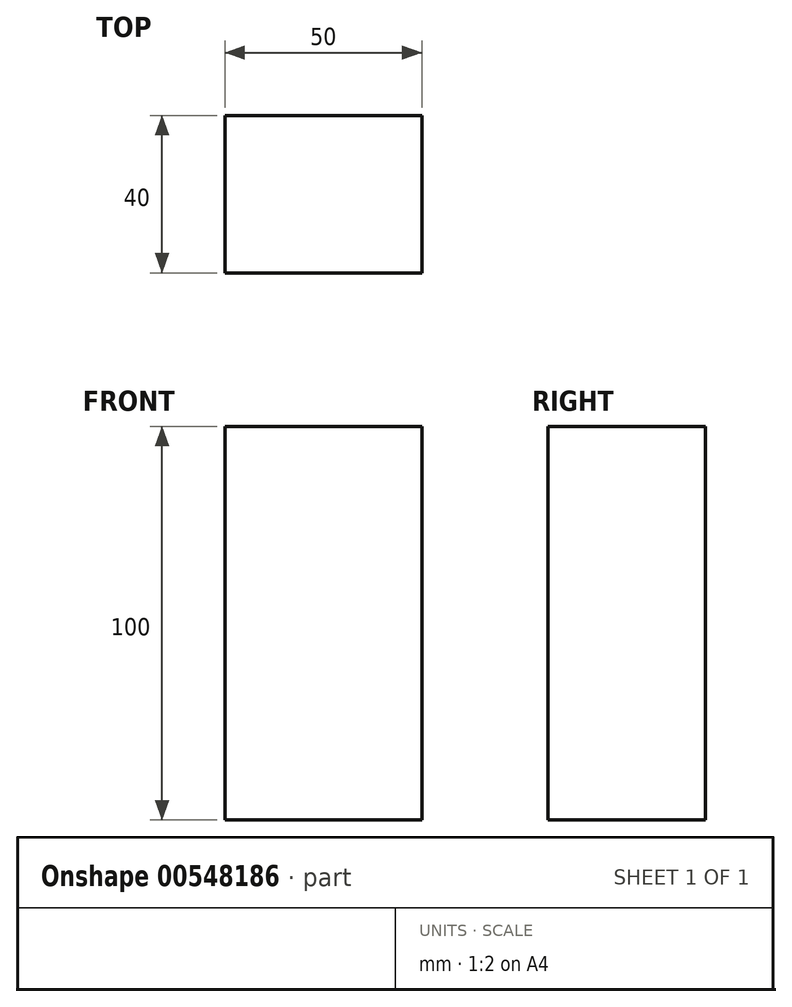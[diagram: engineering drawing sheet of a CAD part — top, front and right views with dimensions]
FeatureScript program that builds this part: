
annotation { "Feature Type Name" : "Feature", "Feature Type Description" : "" }
export const myFeature = defineFeature(function(context is Context, id is Id, definition is map)
    precondition{}
    {
        {
            var Q0;
            Q0=qCreatedBy(makeId("Top.planeOp"),FACE);
            var sketch = newSketch(context, id + "F0", { "sketchPlane" : qUnion([Q0])});
            skLineSegment(sketch, "E0.bottom", {"start": v(0, 0) * mm, "end": v(50, 0) * mm});
            skLineSegment(sketch, "E0.top", {"start": v(0, 40) * mm, "end": v(50, 40) * mm});
            skLineSegment(sketch, "E0.left", {"start": v(0, 0) * mm, "end": v(0, 40) * mm});
            skLineSegment(sketch, "E0.right", {"start": v(50, 0) * mm, "end": v(50, 40) * mm});
            skSolve(sketch);
        }
        {
            var Q0;
            Q0=makeQuery(id+"F0.imprint","IMPRINT",FACE,{"disambiguationData":[TD([[makeQuery(id+"F0.imprint","IMPRINT",EDGE,{"derivedFrom":sQuery(id+"F0.wireOp",EDGE,"E0.bottom")}),1.0]])]});
            extrude(context, id + "F1", {"entities" : qUnion([Q0]), "depth" : 100 * mm, "offsetDistance" : 25 * mm});
        }
    });
